# Revit family: MP40
name_source: partatom
category: Generic Models
revit_build: Autodesk Revit LT 2017 (Build: 20160225_1515(x64)
units: mm (PartAtom-declared; Revit-internal decimal feet)

## family parameters
Always vertical = No
Can host rebar = No
Cut with Voids When Loaded = No
Part Type = Normal
Room Calculation Point = No
Round Connector Dimension = Use Diameter
Shared = No
Work Plane-Based = Yes

## types (1)
- NBS Standard Parameters
    BIMObjectName = metpro_metprolibrary_channelcablesupport_channelbracket
    Default Elevation = 1219 mm
    Description = MP40 Small C Clamp C/W Cone Point
    DurationUnit = year
    Finish = Hot dipped Galvanised
    Keynote = Compliant to LU Standard 10-85
    ManufacturerName = Metpro Ltd
    ManufacturerURL = www.metpro.co.uk
    Material = Steel
    ModelReference = MP40
    NBSDescription = Channel Cable Supports
    NBSReference = 90-55-10/305
    NominalHeight = 40 mm  [stored 0.131234 ft]
    NominalLength = 54 mm  [stored 0.177165 ft]
    NominalWidth = 30 mm  [stored 0.0984252 ft]
    ProductInformation = www.metpro.co.uk/pdf/mp40.pdf
    Uniclass2 = Pr_65_70_11_19
    Version = 1
    WarrantyDurationUnit = 1 year
    Weight = 0.184 Kg

note: [stored X ft] marks values corroborated as IEEE doubles in the binary element streams (Revit-internal decimal feet)

## geometry (parser evidence)
native form markers: Sweep x2
no freeform markers — native parametric forms only
